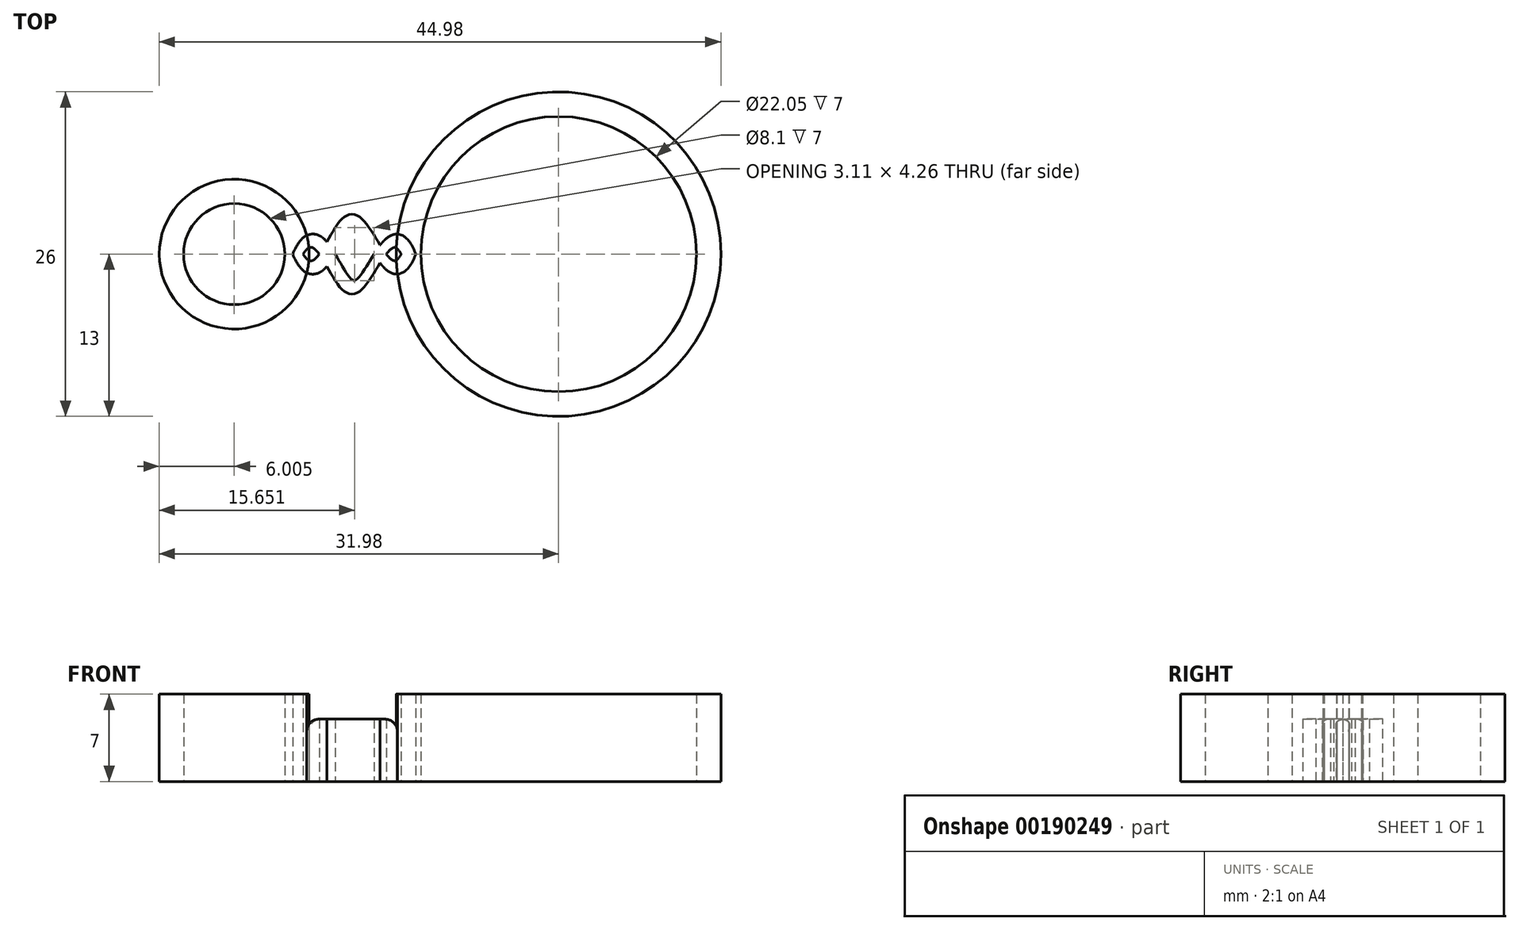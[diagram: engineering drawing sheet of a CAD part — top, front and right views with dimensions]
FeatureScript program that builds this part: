
annotation { "Feature Type Name" : "Feature", "Feature Type Description" : "" }
export const myFeature = defineFeature(function(context is Context, id is Id, definition is map)
    precondition{}
    {
        {
            var Q0;
            Q0=qCreatedBy(makeId("Top.planeOp"),FACE);
            var sketch = newSketch(context, id + "F0", { "sketchPlane" : qUnion([Q0])});
            skCircle(sketch, "E0", {"center": v(0, 0) * mm, "radius": 11.03 * mm});
            skCircle(sketch, "E1", {"center": v(0, 0) * mm, "radius": 13 * mm});
            skCircle(sketch, "E2", {"center": v(-25.97, 0) * mm, "radius": 4.05 * mm});
            skCircle(sketch, "E3", {"center": v(-25.97, 0) * mm, "radius": 6 * mm});
            skLineSegment(sketch, "E4", {"start": v(-22.2, 0) * mm, "end": v(-13, 0) * mm, "construction": true});
            skPoint(sketch, "E5", {"position": v(-17.6, 0) * mm});
            skFitSpline(sketch, "E6.0", {"points": [v(-20.78, 0.67) * mm, v(-20.67, 0.41) * mm, v(-20.45, 0) * mm, v(-20.16, -0.4) * mm, v(-19.98, -0.52) * mm, v(-19.89, -0.55) * mm, v(-19.84, -0.55) * mm, v(-19.78, -0.55) * mm, v(-19.68, -0.5) * mm, v(-19.5, -0.39) * mm, v(-19.26, -0.12) * mm, v(-19, 0.24) * mm, v(-18.74, 0.67) * mm, v(-18.48, 1.13) * mm, v(-18.2, 1.6) * mm, v(-17.94, 2.04) * mm, v(-17.66, 2.45) * mm, v(-17.42, 2.75) * mm, v(-17.2, 2.95) * mm, v(-17.01, 3.07) * mm, v(-16.8, 3.16) * mm, v(-16.55, 3.2) * mm, v(-16.3, 3.16) * mm, v(-16.1, 3.07) * mm, v(-15.9, 2.95) * mm, v(-15.68, 2.76) * mm, v(-15.42, 2.47) * mm, v(-15.13, 2.06) * mm, v(-14.84, 1.61) * mm, v(-14.55, 1.14) * mm, v(-14.27, 0.69) * mm, v(-14, 0.26) * mm, v(-13.72, -0.1) * mm, v(-13.51, -0.33) * mm, v(-13.36, -0.45) * mm, v(-13.28, -0.5) * mm, v(-13.22, -0.52) * mm, v(-13.18, -0.53) * mm, v(-13.14, -0.54) * mm, v(-13.1, -0.53) * mm, v(-13.04, -0.51) * mm, v(-12.96, -0.46) * mm, v(-12.82, -0.32) * mm, v(-12.6, 0) * mm, v(-12.42, 0.41) * mm, v(-12.32, 0.67) * mm]});
            skFitSpline(sketch, "E7.0", {"points": [v(-21.34, 0.1) * mm, v(-21.21, -0.18) * mm, v(-20.97, -0.66) * mm, v(-20.59, -1.18) * mm, v(-20.23, -1.46) * mm, v(-19.9, -1.58) * mm, v(-19.64, -1.6) * mm, v(-19.4, -1.57) * mm, v(-19.1, -1.45) * mm, v(-18.78, -1.22) * mm, v(-18.46, -0.86) * mm, v(-18.16, -0.45) * mm, v(-17.88, 0) * mm, v(-17.6, 0.48) * mm, v(-17.34, 0.94) * mm, v(-17.08, 1.37) * mm, v(-16.84, 1.73) * mm, v(-16.65, 1.95) * mm, v(-16.52, 2.06) * mm, v(-16.44, 2.1) * mm, v(-16.4, 2.13) * mm, v(-16.37, 2.13) * mm, v(-16.35, 2.13) * mm, v(-16.3, 2.1) * mm, v(-16.21, 2.06) * mm, v(-16.08, 1.94) * mm, v(-15.88, 1.72) * mm, v(-15.62, 1.36) * mm, v(-15.34, 0.93) * mm, v(-15.06, 0.47) * mm, v(-14.78, 0) * mm, v(-14.48, -0.45) * mm, v(-14.17, -0.87) * mm, v(-13.9, -1.17) * mm, v(-13.65, -1.36) * mm, v(-13.46, -1.48) * mm, v(-13.27, -1.56) * mm, v(-13.13, -1.59) * mm, v(-13.05, -1.6) * mm, v(-13, -1.6) * mm, v(-12.93, -1.6) * mm, v(-12.86, -1.6) * mm, v(-12.8, -1.59) * mm, v(-12.73, -1.57) * mm, v(-12.67, -1.56) * mm, v(-12.6, -1.53) * mm, v(-12.45, -1.46) * mm, v(-12.27, -1.34) * mm, v(-12, -1.08) * mm, v(-11.72, -0.64) * mm, v(-11.5, -0.16) * mm, v(-11.4, 0.12) * mm]});
            skPoint(sketch, "E8", {"position": v(-20.16, -1.48) * mm});
            skPoint(sketch, "E9", {"position": v(-12.9, -1.6) * mm});
            skFitSpline(sketch, "E10.MirrorCS", {"points": [v(-21.34, -0.1) * mm, v(-21.21, 0.18) * mm, v(-20.97, 0.66) * mm, v(-20.59, 1.18) * mm, v(-20.23, 1.46) * mm, v(-19.9, 1.58) * mm, v(-19.64, 1.6) * mm, v(-19.4, 1.57) * mm, v(-19.1, 1.45) * mm, v(-18.78, 1.22) * mm, v(-18.46, 0.86) * mm, v(-18.16, 0.45) * mm, v(-17.88, 0) * mm, v(-17.6, -0.48) * mm, v(-17.34, -0.94) * mm, v(-17.08, -1.37) * mm, v(-16.84, -1.73) * mm, v(-16.65, -1.95) * mm, v(-16.52, -2.06) * mm, v(-16.44, -2.1) * mm, v(-16.4, -2.13) * mm, v(-16.37, -2.13) * mm, v(-16.35, -2.13) * mm, v(-16.3, -2.1) * mm, v(-16.21, -2.06) * mm, v(-16.08, -1.94) * mm, v(-15.88, -1.72) * mm, v(-15.62, -1.36) * mm, v(-15.34, -0.93) * mm, v(-15.06, -0.47) * mm, v(-14.78, 0) * mm, v(-14.48, 0.45) * mm, v(-14.17, 0.87) * mm, v(-13.9, 1.17) * mm, v(-13.65, 1.36) * mm, v(-13.46, 1.48) * mm, v(-13.27, 1.56) * mm, v(-13.13, 1.59) * mm, v(-13.05, 1.6) * mm, v(-13, 1.6) * mm, v(-12.93, 1.6) * mm, v(-12.86, 1.6) * mm, v(-12.8, 1.59) * mm, v(-12.73, 1.57) * mm, v(-12.67, 1.56) * mm, v(-12.6, 1.53) * mm, v(-12.45, 1.46) * mm, v(-12.27, 1.34) * mm, v(-12, 1.08) * mm, v(-11.72, 0.64) * mm, v(-11.5, 0.16) * mm, v(-11.4, -0.12) * mm]});
            skFitSpline(sketch, "E11.MirrorCS", {"points": [v(-20.78, -0.67) * mm, v(-20.67, -0.41) * mm, v(-20.45, 0) * mm, v(-20.16, 0.4) * mm, v(-19.98, 0.52) * mm, v(-19.89, 0.55) * mm, v(-19.84, 0.55) * mm, v(-19.78, 0.55) * mm, v(-19.68, 0.5) * mm, v(-19.5, 0.39) * mm, v(-19.26, 0.12) * mm, v(-19, -0.24) * mm, v(-18.74, -0.67) * mm, v(-18.48, -1.13) * mm, v(-18.2, -1.6) * mm, v(-17.94, -2.04) * mm, v(-17.66, -2.45) * mm, v(-17.42, -2.75) * mm, v(-17.2, -2.95) * mm, v(-17.01, -3.07) * mm, v(-16.8, -3.16) * mm, v(-16.55, -3.2) * mm, v(-16.3, -3.16) * mm, v(-16.1, -3.07) * mm, v(-15.9, -2.95) * mm, v(-15.68, -2.76) * mm, v(-15.42, -2.47) * mm, v(-15.13, -2.06) * mm, v(-14.84, -1.61) * mm, v(-14.55, -1.14) * mm, v(-14.27, -0.69) * mm, v(-14, -0.26) * mm, v(-13.72, 0.1) * mm, v(-13.51, 0.33) * mm, v(-13.36, 0.45) * mm, v(-13.28, 0.5) * mm, v(-13.22, 0.52) * mm, v(-13.18, 0.53) * mm, v(-13.14, 0.54) * mm, v(-13.1, 0.53) * mm, v(-13.04, 0.51) * mm, v(-12.96, 0.46) * mm, v(-12.82, 0.32) * mm, v(-12.6, 0) * mm, v(-12.42, -0.41) * mm, v(-12.32, -0.67) * mm]});
            skSolve(sketch);
        }
        {
            var Q0;
            {var subQ0=sQuery(id+"F0.wireOp",EDGE,"E11.MirrorCS");var subQ1=sQuery(id+"F0.wireOp",EDGE,"E6.0");var subQ2=makeQuery(id+"F0.imprint","INTERSECT",VERTEX,{"disambiguationData":[OD(2.0)],"derivedFrom":[subQ1,subQ0]});Q0=makeQuery(id+"F0.imprint","IMPRINT",FACE,{"disambiguationData":[TD([[makeQuery(id+"F0.imprint","IMPRINT",EDGE,{"disambiguationData":[TD([[subQ2,-1.0]])],"derivedFrom":subQ1}),-1.0]])]});}
            var Q1;
            {var subQ0=sQuery(id+"F0.wireOp",EDGE,"E10.MirrorCS");var subQ1=sQuery(id+"F0.wireOp",EDGE,"E6.0");var subQ2=makeQuery(id+"F0.imprint","INTERSECT",VERTEX,{"disambiguationData":[OD(0.0)],"derivedFrom":[subQ1,subQ0]});Q1=makeQuery(id+"F0.imprint","IMPRINT",FACE,{"disambiguationData":[TD([[makeQuery(id+"F0.imprint","IMPRINT",EDGE,{"disambiguationData":[TD([[subQ2,-1.0]])],"derivedFrom":subQ1}),-1.0]])]});}
            var Q2;
            {var subQ0=sQuery(id+"F0.wireOp",EDGE,"E10.MirrorCS");var subQ1=sQuery(id+"F0.wireOp",EDGE,"E6.0");var subQ2=makeQuery(id+"F0.imprint","INTERSECT",VERTEX,{"disambiguationData":[OD(1.0)],"derivedFrom":[subQ1,subQ0]});Q2=makeQuery(id+"F0.imprint","IMPRINT",FACE,{"disambiguationData":[TD([[makeQuery(id+"F0.imprint","IMPRINT",EDGE,{"disambiguationData":[TD([[subQ2,-1.0]])],"derivedFrom":subQ1}),-1.0]])]});}
            var Q3;
            {var subQ0=sQuery(id+"F0.wireOp",EDGE,"E10.MirrorCS");var subQ1=sQuery(id+"F0.wireOp",EDGE,"E6.0");var subQ2=makeQuery(id+"F0.imprint","INTERSECT",VERTEX,{"disambiguationData":[OD(0.0)],"derivedFrom":[subQ1,subQ0]});Q3=makeQuery(id+"F0.imprint","IMPRINT",FACE,{"disambiguationData":[TD([[makeQuery(id+"F0.imprint","IMPRINT",EDGE,{"disambiguationData":[TD([[subQ2,-1.0]])],"derivedFrom":subQ1}),-1.0]])]});}
            var Q4;
            {var subQ0=sQuery(id+"F0.wireOp",EDGE,"E7.0");var subQ1=sQuery(id+"F0.wireOp",EDGE,"E1");var subQ2=makeQuery(id+"F0.imprint","INTERSECT",VERTEX,{"derivedFrom":[subQ1,subQ0]});Q4=makeQuery(id+"F0.imprint","IMPRINT",FACE,{"disambiguationData":[TD([[makeQuery(id+"F0.imprint","IMPRINT",EDGE,{"disambiguationData":[TD([[subQ2,1.0]])],"derivedFrom":subQ1}),-1.0]])]});}
            var Q5;
            {var subQ0=sQuery(id+"F0.wireOp",EDGE,"E10.MirrorCS");var subQ1=sQuery(id+"F0.wireOp",EDGE,"E6.0");var subQ2=makeQuery(id+"F0.imprint","INTERSECT",VERTEX,{"disambiguationData":[OD(1.0)],"derivedFrom":[subQ1,subQ0]});Q5=makeQuery(id+"F0.imprint","IMPRINT",FACE,{"disambiguationData":[TD([[makeQuery(id+"F0.imprint","IMPRINT",EDGE,{"disambiguationData":[TD([[subQ2,-1.0]])],"derivedFrom":subQ1}),-1.0]])]});}
            var Q6;
            {var subQ0=sQuery(id+"F0.wireOp",EDGE,"E11.MirrorCS");var subQ1=sQuery(id+"F0.wireOp",EDGE,"E7.0");var subQ2=makeQuery(id+"F0.imprint","INTERSECT",VERTEX,{"disambiguationData":[OD(0.0)],"derivedFrom":[subQ1,subQ0]});Q6=makeQuery(id+"F0.imprint","IMPRINT",FACE,{"disambiguationData":[TD([[makeQuery(id+"F0.imprint","IMPRINT",EDGE,{"disambiguationData":[TD([[subQ2,-1.0]])],"derivedFrom":subQ1}),-1.0]])]});}
            var Q7;
            {var subQ0=sQuery(id+"F0.wireOp",EDGE,"E11.MirrorCS");var subQ1=sQuery(id+"F0.wireOp",EDGE,"E6.0");var subQ2=makeQuery(id+"F0.imprint","INTERSECT",VERTEX,{"disambiguationData":[OD(2.0)],"derivedFrom":[subQ1,subQ0]});Q7=makeQuery(id+"F0.imprint","IMPRINT",FACE,{"disambiguationData":[TD([[makeQuery(id+"F0.imprint","IMPRINT",EDGE,{"disambiguationData":[TD([[subQ2,-1.0]])],"derivedFrom":subQ1}),-1.0]])]});}
            var Q8;
            {var subQ0=sQuery(id+"F0.wireOp",EDGE,"E7.0");var subQ1=sQuery(id+"F0.wireOp",EDGE,"E3");var subQ2=makeQuery(id+"F0.imprint","INTERSECT",VERTEX,{"derivedFrom":[subQ1,subQ0]});Q8=makeQuery(id+"F0.imprint","IMPRINT",FACE,{"disambiguationData":[TD([[makeQuery(id+"F0.imprint","IMPRINT",EDGE,{"disambiguationData":[TD([[subQ2,-1.0]])],"derivedFrom":subQ1}),-1.0]])]});}
            var Q9;
            {var subQ0=sQuery(id+"F0.wireOp",EDGE,"E10.MirrorCS");var subQ1=sQuery(id+"F0.wireOp",EDGE,"E3");var subQ2=makeQuery(id+"F0.imprint","INTERSECT",VERTEX,{"derivedFrom":[subQ1,subQ0]});Q9=makeQuery(id+"F0.imprint","IMPRINT",FACE,{"disambiguationData":[TD([[makeQuery(id+"F0.imprint","IMPRINT",EDGE,{"disambiguationData":[TD([[subQ2,1.0]])],"derivedFrom":subQ1}),-1.0]])]});}
            var Q10;
            {var subQ0=sQuery(id+"F0.wireOp",EDGE,"E10.MirrorCS");var subQ1=sQuery(id+"F0.wireOp",EDGE,"E1");var subQ2=makeQuery(id+"F0.imprint","INTERSECT",VERTEX,{"derivedFrom":[subQ1,subQ0]});Q10=makeQuery(id+"F0.imprint","IMPRINT",FACE,{"disambiguationData":[TD([[makeQuery(id+"F0.imprint","IMPRINT",EDGE,{"disambiguationData":[TD([[subQ2,-1.0]])],"derivedFrom":subQ1}),-1.0]])]});}
            extrude(context, id + "F1", {"entities" : qUnion([Q0, Q1, Q2, Q3, Q4, Q5, Q6, Q7, Q8, Q9, Q10]), "offsetDistance" : 25 * mm, "depth" : 5 * mm});
        }
        {
            var Q0;
            Q0=makeQuery(id+"F0.imprint","IMPRINT",FACE,{"disambiguationData":[TD([[makeQuery(id+"F0.imprint","IMPRINT",EDGE,{"derivedFrom":sQuery(id+"F0.wireOp",EDGE,"E2")}),-1.0]])]});
            var Q1;
            Q1=makeQuery(id+"F0.imprint","IMPRINT",FACE,{"disambiguationData":[TD([[makeQuery(id+"F0.imprint","IMPRINT",EDGE,{"derivedFrom":sQuery(id+"F0.wireOp",EDGE,"E0")}),-1.0]])]});
            var Q2;
            {var subQ0=sQuery(id+"F0.wireOp",EDGE,"E11.MirrorCS");var subQ1=sQuery(id+"F0.wireOp",EDGE,"E3");var subQ2=makeQuery(id+"F0.imprint","INTERSECT",VERTEX,{"derivedFrom":[subQ1,subQ0]});Q2=makeQuery(id+"F0.imprint","IMPRINT",FACE,{"disambiguationData":[TD([[makeQuery(id+"F0.imprint","IMPRINT",EDGE,{"disambiguationData":[TD([[subQ2,1.0]])],"derivedFrom":subQ1}),1.0]])]});}
            var Q3;
            {var subQ0=sQuery(id+"F0.wireOp",EDGE,"E11.MirrorCS");var subQ1=sQuery(id+"F0.wireOp",EDGE,"E1");var subQ2=makeQuery(id+"F0.imprint","INTERSECT",VERTEX,{"derivedFrom":[subQ1,subQ0]});Q3=makeQuery(id+"F0.imprint","IMPRINT",FACE,{"disambiguationData":[TD([[makeQuery(id+"F0.imprint","IMPRINT",EDGE,{"disambiguationData":[TD([[subQ2,-1.0]])],"derivedFrom":subQ1}),1.0]])]});}
            extrude(context, id + "F2", {"entities" : qUnion([Q0, Q1, Q2, Q3]), "operationType" : NewBodyOperationType.ADD, "depth" : 7 * mm});
        }
        {
            var Q0;
            {var subQ0=sQuery(id+"F0.wireOp",EDGE,"E3");Q0=makeQuery(id+"F1.opExtrude","CAP_EDGE",EDGE,{"disambiguationData":[OSD([subQ0]),TDD([makeQuery(id+"F0.imprint","IMPRINT",EDGE,{"disambiguationData":[TD([[makeQuery(id+"F0.imprint","INTERSECT",VERTEX,{"derivedFrom":[subQ0,sQuery(id+"F0.wireOp",EDGE,"E7.0")]}),-1.0]])],"derivedFrom":subQ0})])],"isStart":false});}
            var Q1;
            {var subQ0=sQuery(id+"F0.wireOp",EDGE,"E1");Q1=makeQuery(id+"F1.opExtrude","CAP_EDGE",EDGE,{"disambiguationData":[OSD([subQ0]),TDD([makeQuery(id+"F0.imprint","IMPRINT",EDGE,{"disambiguationData":[TD([[makeQuery(id+"F0.imprint","INTERSECT",VERTEX,{"derivedFrom":[subQ0,sQuery(id+"F0.wireOp",EDGE,"E7.0")]}),1.0]])],"derivedFrom":subQ0})])],"isStart":false});}
            fillet(context, id + "F3", {"entities" : qUnion([Q0, Q1]), "radius" : 1 * mm, "tangentPropagation" : true, "allowEdgeOverflow" : false});
        }
    });
